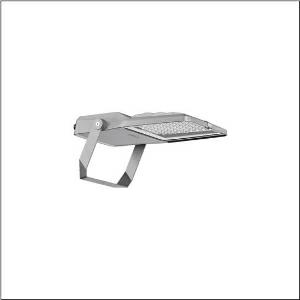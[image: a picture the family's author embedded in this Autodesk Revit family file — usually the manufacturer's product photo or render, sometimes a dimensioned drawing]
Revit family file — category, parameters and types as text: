
# Revit family: floodlight_fl_21_iq_mini___pl43_5xa7772b2a1a_654d
name_source: partatom
category: Lighting Fixtures
units: mm (PartAtom-declared; Revit-internal decimal feet)

## family parameters
Cut with Voids When Loaded = No
Host = Face
Light Source = No
Part Type = Normal
Room Calculation Point = No
Round Connector Dimension = Use Diameter
Shared = No

## types (1)
- --- (1 x LED, 6400 lm, 45.5 W, 3000K)
    Apparent Load = 46 VA
    CIE Flux Codes = 27 78 99 100 100
    Color Rendering = 70
    Color Temperature = 3000K
    Default Elevation = 1800 mm
    Description = Floodlight FL 21 iQ mini, floodlight, primary light control with lens, of PMMA, primary optical cover: protective disc, of toughened safety glass, transparent, light distribution: PL43, light emission: direct distribution, installation type: surface-mounted, LED, High Power LED, rated luminous flux: 6.400lm, luminous efficacy: 141lm/W, light colour: 730, colour temperature: 3000K, control gear: iQ Street-Remote/DALI, control: Street-Remote, Auto-Match, Temp-Guard, Night-Set, Smart-Wire, Desk-Remote (wireless, voltage-free reading and setting of iQ features in the workshop via application-optimized NFC function/RFID function), optimised constant luminous flux control (CLO 2.0), with terminal, 6-pole, mains connection: 220..240V, AC, 50/60Hz, start of lifetime: 46W, end of service life: 48W, reduction: 22W, luminaire housing, of diecast aluminium, powder-coated, Siteco® metallic grey (DB 702S), corrosivity category C5 mid according to DIN EN ISO 12944, suitable for swimming pools, chlorine-resistant, sealing non-destructively replaceable, mounting bracket, of steel, galvanised, powder-coated, Siteco® metallic grey (DB 702S), protection rating (complete): IP66, insulation class (complete): insulation class II (safety insulation), certification: CE, ENEC, VDE, protection symbol: D, impact resistance: IK08, permissible operating ambient temperature: -40..+40°C, permissible operating ambient temperature for outdoor applications: -40..+50°C, standard: DIN EN 12944, LABS conformity tested according to VDMA 24364:2018-05, packaging unit: 1 piece

Light Distribution: PL43
    Height = 70 mm
    Lamp = 1 x LED
    Lamp Light Flux = 6400 lm
    Lamp Power = 45.5 W
    Lamp count = 1
    Length = 485 mm
    Luminous efficacy = 141 lm/W
    Manufacturer = Siteco
    ModVariant = No
    Model = 5XA7772B2A1A
    Number of Poles = 1
    OnlyDefault = Yes
    Power Factor = 1
    Product Name = Floodlight FL 21 iQ mini | PL43
    Product group = floodlight | pylon annexe
    ProductGroupID = 6200
    Protection Class = Protection class II
    Protection Degree = IP 66
    RLX_Detail_Level = 1
    RLX_Emergency_Light_Flux = 0 lm
    RLX_Emergency_Type = 0
    RLX_Emergency_Type_DB = No
    RlxData = <blob elided: 96421 chars, md5=e2d22b44>
    Socket = socket
    Standby Power = 0 W
    System Light Flux = 6400 lm
    System Power = 46 W
    Type Comments = factory setting: luminous flux: 100 % | dim-lin: 254 | 463 mA
    Type Image = l_1006845.jpg
    URL = http://relux.com
    VarID = @adj_162970
    Voltage = 0 V
    Weight = 0.00 kg
    Width = 337 mm

## geometry (parser evidence)
native form markers: Blend x4, Sweep x13
no freeform markers — native parametric forms only
